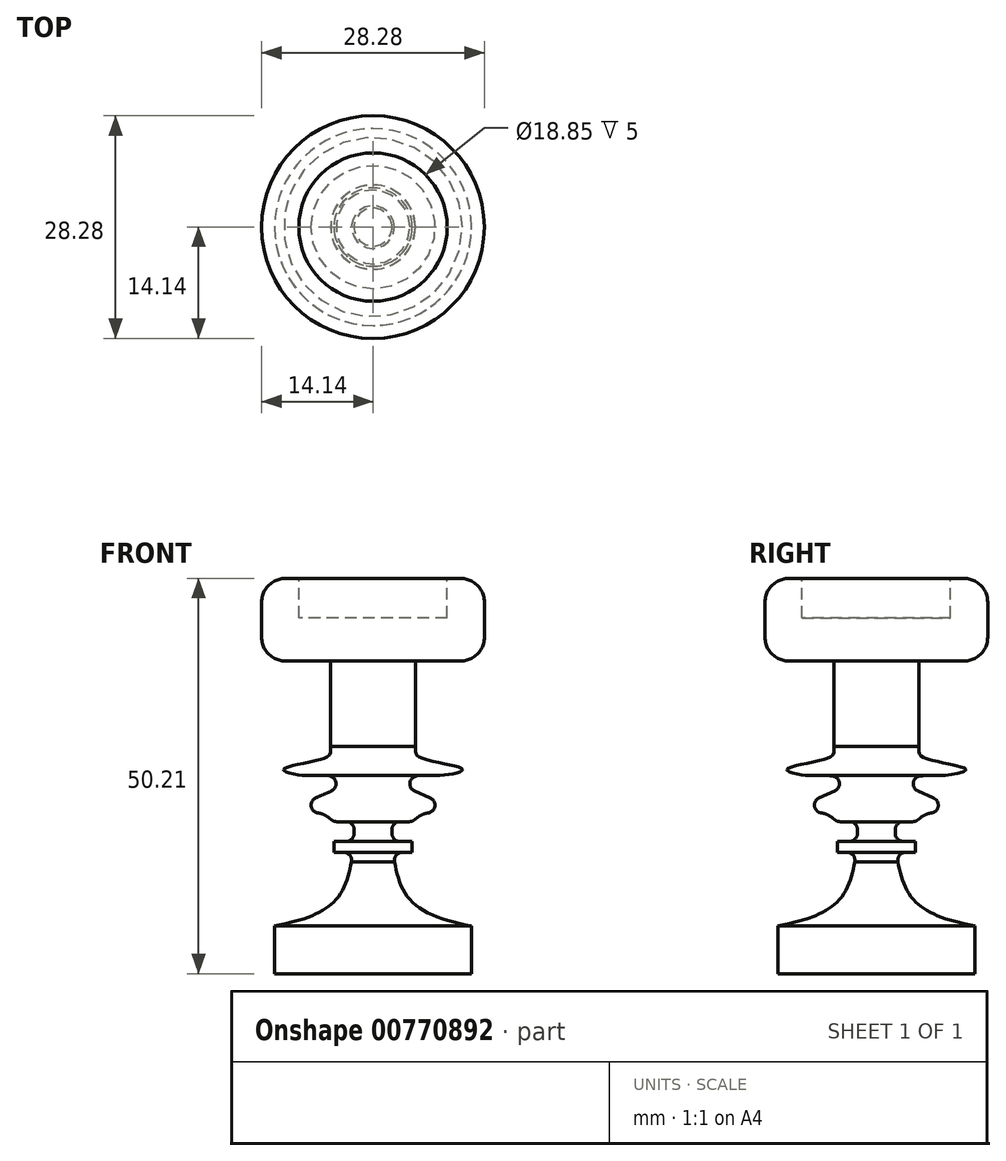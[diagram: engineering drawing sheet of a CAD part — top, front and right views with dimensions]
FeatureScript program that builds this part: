
annotation { "Feature Type Name" : "Feature", "Feature Type Description" : "" }
export const myFeature = defineFeature(function(context is Context, id is Id, definition is map)
    precondition{}
    {
        {
            var Q0;
            Q0=qCreatedBy(makeId("Front.planeOp"),FACE);
            var sketch = newSketch(context, id + "F0", { "sketchPlane" : qUnion([Q0])});
            skLineSegment(sketch, "E0.bottom", {"start": v(0, 0) * mm, "end": v(20, 0) * mm});
            skLineSegment(sketch, "E0.right", {"start": v(20, 0) * mm, "end": v(20, 5) * mm});
            skFitSpline(sketch, "E1", {"points": [v(20, 5) * mm, v(5.27, 8.84) * mm, v(2.52, 15.41) * mm], "startDerivative": vector(-30.16, 3.58) * mm, "endDerivative": vector(-3.11, 18.15) * mm});
            skLineSegment(sketch, "E2.bottom", {"start": v(2.52, 15.41) * mm, "end": v(4.97, 15.41) * mm});
            skLineSegment(sketch, "E2.right", {"start": v(4.97, 15.41) * mm, "end": v(4.97, 16.8) * mm});
            skLineSegment(sketch, "E3", {"start": v(6.26, 20.35) * mm, "end": v(10.63, 20.86) * mm});
            skLineSegment(sketch, "E4", {"start": v(10.63, 20.86) * mm, "end": v(2.82, 24.3) * mm});
            skFitSpline(sketch, "E5", {"points": [v(2.82, 24.3) * mm, v(8.68, 25.2) * mm, v(11.36, 26) * mm, v(5.8, 27.58) * mm, v(5.38, 28.85) * mm, v(2.82, 33.13) * mm, v(-32.06, 38.18) * mm], "startDerivative": vector(58.6, 24.99) * mm, "endDerivative": vector(-147.9, 1.56) * mm});
            skLineSegment(sketch, "E6", {"start": v(5.38, 28.85) * mm, "end": v(5.38, 39.73) * mm});
            skLineSegment(sketch, "E7", {"start": v(5.38, 39.73) * mm, "end": v(14.14, 39.73) * mm});
            skLineSegment(sketch, "E8", {"start": v(14.14, 39.73) * mm, "end": v(14.14, 50.21) * mm});
            skLineSegment(sketch, "E9", {"start": v(14.14, 50.21) * mm, "end": v(0, 50.21) * mm});
            skLineSegment(sketch, "E10", {"start": v(0, 50.21) * mm, "end": v(0, 0) * mm});
            skLineSegment(sketch, "E11", {"start": v(4.97, 16.8) * mm, "end": v(2.4, 16.82) * mm});
            skLineSegment(sketch, "E12", {"start": v(2.4, 16.82) * mm, "end": v(2.4, 19.32) * mm});
            skLineSegment(sketch, "E13", {"start": v(2.4, 19.32) * mm, "end": v(4.97, 19.32) * mm});
            skLineSegment(sketch, "E14", {"start": v(4.97, 19.32) * mm, "end": v(6.26, 20.35) * mm});
            skSolve(sketch);
        }
        {
            var Q0;
            Q0=qSketchRegion(id+"F0",true);
            var Q1;
            Q1=sQuery(id+"F0.wireOp",EDGE,"E10");
            revolve(context, id + "F1", {"surfaceOperationType" : NewSurfaceOperationType.NEW, "entities" : qUnion([Q0]), "axis" : qUnion([Q1]), "revolveType" : RevolveType.FULL});
        }
        {
            var Q0;
            Q0=makeQuery(id+"F1.opRevolve","SWEPT_FACE",FACE,{"disambiguationData":[OSD([sQuery(id+"F0.wireOp",EDGE,"E9")])]});
            var sketch = newSketch(context, id + "F2", { "sketchPlane" : qUnion([Q0])});
            skCircle(sketch, "E15", {"center": v(0, 0) * mm, "radius": 9.42 * mm});
            skSolve(sketch);
        }
        {
            var Q0;
            Q0=qSketchRegion(id+"F2",true);
            extrude(context, id + "F3", {"entities" : qUnion([Q0]), "operationType" : NewBodyOperationType.REMOVE, "oppositeDirection" : true, "depth" : 5 * mm, "offsetDistance" : 25 * mm});
        }
        {
            var Q0;
            Q0=makeQuery(id+"F1.opRevolve","SWEPT_EDGE",EDGE,{"disambiguationData":[OSD([sQuery(id+"F0.wireOp",EDGE,"E7"),sQuery(id+"F0.wireOp",EDGE,"E8")])]});
            fillet(context, id + "F4", {"entities" : qUnion([Q0]), "radius" : 3 * mm, "tangentPropagation" : true, "allowEdgeOverflow" : false});
        }
        {
            var Q0;
            Q0=makeQuery(id+"F1.opRevolve","SWEPT_EDGE",EDGE,{"disambiguationData":[OSD([sQuery(id+"F0.wireOp",EDGE,"E8"),sQuery(id+"F0.wireOp",EDGE,"E9")])]});
            fillet(context, id + "F5", {"entities" : qUnion([Q0]), "radius" : 3 * mm, "tangentPropagation" : true, "allowEdgeOverflow" : false});
        }
        {
            var Q0;
            Q0=makeQuery(id+"F1.opRevolve","SWEPT_EDGE",EDGE,{"disambiguationData":[OSD([sQuery(id+"F0.wireOp",EDGE,"E1"),sQuery(id+"F0.wireOp",EDGE,"E2.bottom")])]});
            fillet(context, id + "F6", {"entities" : qUnion([Q0]), "radius" : 1 * mm, "tangentPropagation" : true, "allowEdgeOverflow" : false});
        }
        {
            var Q0;
            Q0=makeQuery(id+"F1.opRevolve","SWEPT_EDGE",EDGE,{"disambiguationData":[OSD([sQuery(id+"F0.wireOp",EDGE,"E11"),sQuery(id+"F0.wireOp",EDGE,"E12")])]});
            fillet(context, id + "F7", {"entities" : qUnion([Q0]), "radius" : 1 * mm, "tangentPropagation" : true, "allowEdgeOverflow" : false});
        }
        {
            var Q0;
            Q0=makeQuery(id+"F1.opRevolve","SWEPT_EDGE",EDGE,{"disambiguationData":[OSD([sQuery(id+"F0.wireOp",EDGE,"E12"),sQuery(id+"F0.wireOp",EDGE,"E13")])]});
            fillet(context, id + "F8", {"entities" : qUnion([Q0]), "radius" : 1 * mm, "tangentPropagation" : true, "allowEdgeOverflow" : false});
        }
        {
            var Q0;
            Q0=makeQuery(id+"F1.opRevolve","SWEPT_EDGE",EDGE,{"disambiguationData":[OSD([sQuery(id+"F0.wireOp",EDGE,"E13"),sQuery(id+"F0.wireOp",EDGE,"E14")])]});
            fillet(context, id + "F9", {"entities" : qUnion([Q0]), "radius" : 1 * mm, "tangentPropagation" : true, "allowEdgeOverflow" : false});
        }
        {
            var Q0;
            Q0=makeQuery(id+"F1.opRevolve","SWEPT_EDGE",EDGE,{"disambiguationData":[OSD([sQuery(id+"F0.wireOp",EDGE,"E3"),sQuery(id+"F0.wireOp",EDGE,"E14")])]});
            fillet(context, id + "F10", {"entities" : qUnion([Q0]), "radius" : 3 * mm, "tangentPropagation" : true, "allowEdgeOverflow" : false});
        }
        {
            var Q0;
            Q0=makeQuery(id+"F1.opRevolve","SWEPT_EDGE",EDGE,{"disambiguationData":[OSD([sQuery(id+"F0.wireOp",EDGE,"E3"),sQuery(id+"F0.wireOp",EDGE,"E4")])]});
            fillet(context, id + "F11", {"entities" : qUnion([Q0]), "radius" : 1 * mm, "tangentPropagation" : true, "allowEdgeOverflow" : false});
        }
        {
            var Q0;
            Q0=makeQuery(id+"F1.opRevolve","SWEPT_EDGE",EDGE,{"disambiguationData":[OSD([sQuery(id+"F0.wireOp",EDGE,"E4"),sQuery(id+"F0.wireOp",EDGE,"E5")])]});
            fillet(context, id + "F12", {"entities" : qUnion([Q0]), "radius" : 1 * mm, "tangentPropagation" : true, "allowEdgeOverflow" : false});
        }
        {
            var Q0;
            Q0=makeQuery(id+"F1.opRevolve","SWEPT_FACE",FACE,{"disambiguationData":[OSD([sQuery(id+"F0.wireOp",EDGE,"E0.bottom")])]});
            var sketch = newSketch(context, id + "F13", { "sketchPlane" : qUnion([Q0])});
            skCircle(sketch, "E16", {"center": v(0, 0) * mm, "radius": 12.5 * mm});
            skSolve(sketch);
        }
        {
            var Q0;
            Q0=makeQuery(id+"F13.imprint","IMPRINT",FACE,{"disambiguationData":[TD([[makeQuery(id+"F13.imprint","IMPRINT",EDGE,{"derivedFrom":sQuery(id+"F13.wireOp",EDGE,"E16")}),-1.0]])]});
            extrude(context, id + "F14", {"entities" : qUnion([Q0]), "operationType" : NewBodyOperationType.REMOVE, "oppositeDirection" : true, "depth" : 25 * mm, "offsetDistance" : 25 * mm});
        }
    });
